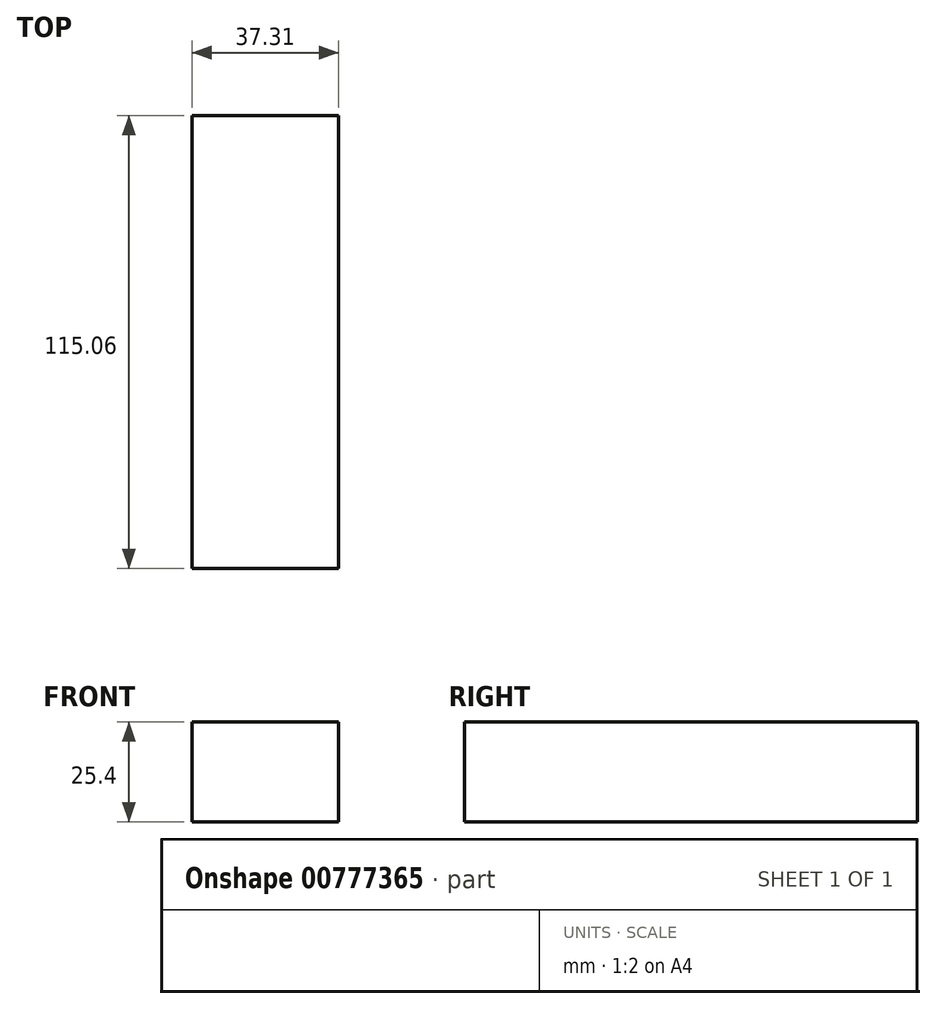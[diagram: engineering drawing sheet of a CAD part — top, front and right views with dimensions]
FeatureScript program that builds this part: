
annotation { "Feature Type Name" : "Feature", "Feature Type Description" : "" }
export const myFeature = defineFeature(function(context is Context, id is Id, definition is map)
    precondition{}
    {
        {
            var Q0;
            Q0=qCreatedBy(makeId("Top.planeOp"),FACE);
            var sketch = newSketch(context, id + "F0", { "sketchPlane" : qUnion([Q0])});
            skLineSegment(sketch, "E0.bottom", {"start": v(-24.05, -41.07) * mm, "end": v(13.26, -41.07) * mm});
            skLineSegment(sketch, "E0.top", {"start": v(-24.05, 73.99) * mm, "end": v(13.26, 73.99) * mm});
            skLineSegment(sketch, "E0.left", {"start": v(-24.05, -41.07) * mm, "end": v(-24.05, 73.99) * mm});
            skLineSegment(sketch, "E0.right", {"start": v(13.26, -41.07) * mm, "end": v(13.26, 73.99) * mm});
            skSolve(sketch);
        }
        {
            var Q0;
            Q0=makeQuery(id+"F0.imprint","IMPRINT",FACE,{"disambiguationData":[TD([[makeQuery(id+"F0.imprint","IMPRINT",EDGE,{"derivedFrom":sQuery(id+"F0.wireOp",EDGE,"E0.bottom")}),1.0]])]});
            extrude(context, id + "F1", {"entities" : qUnion([Q0]), "depth" : 25.4 * mm, "offsetDistance" : 25.4 * mm});
        }
    });
